# Revit family: Power-ModularDevices-GEWISS-90AM-CONTACTORS_MANUAL_COMMAND_20A
name_source: partatom
category: Apparecchi elettrici
revit_build: Autodesk Revit 2016 (Build: 20161004_0715(x64)
units: mm (PartAtom-declared; Revit-internal decimal feet)

## family parameters
Condiviso = No
Host = Superficie
Mantenere orientamento annotazione = Sì
Numero OmniClass = 23.80.30.00
Punto di calcolo locali = Sì
Quota connettore circolare = Usa diametro
Taglio con vuoti quando caricato = No
Tipo di parte = Normale
Titolo OmniClass = Distribution Devices

## types (4) — shared parameters
A = 18 mm  [stored 0.0590551 ft]
B = 85 mm  [stored 0.278871 ft]
C = 65 mm  [stored 0.213255 ft]
Catalogue = POWER
Catalogue Range = 90 AM
Control = Manual
D = 45 mm  [stored 0.147638 ft]
Electrocod = 1712
Fin_Amperometro = <Per categoria>
IDF = 7106f995-c053-4fad-b690-0f915b23fb57
IDT = 203b0cdd-a3f8-4527-9efa-be9d5b2ce0ff
Immagine tipo = GWD6744.jpg
No. Chorus modules = 1
Numero poli = 1
Potenza in Watt = 0 V
Produttore = GEWISS S.p.A.
Prospetto di default = 1219 mm
Rated current (AC-1/AC-7a) = 20 A - CTRM20
TEXT LABEL = A
Technical sheet = https://www.gewiss.com
URL = https://www.gewiss.com
Version file RFA = 18.0

## per-type parameters (varying)
| type | Control coil voltage (V) | Descrizione | EAN code | Modello |
| GWD6741 - CONTACTOR D/N 20A 2NO 24V 1M | 24Vac | CONTACTOR D/N 20A 2NO 24V 1M | 8011564809383 | GWD6741 |
| GWD6742 - CONTACTOR D/N 20A 2NO 230V 1M | 230Vac | CONTACTOR D/N 20A 2NO 230V 1M | 8011564809390 | GWD6742 |
| GWD6743 - CONTACTOR D/N 20A 2NC 230V 1M | 230Vac | CONTACTOR D/N 20A 2NC 230V 1M | 8011564809406 | GWD6743 |
| GWD6744 - CONTACTOR D/N 20A 1NO+1NC 230V 1M | 230Vac | CONTACTOR D/N 20A 1NO+1NC 230V 1M | 8011564809413 | GWD6744 |

note: [stored X ft] marks values corroborated as IEEE doubles in the binary element streams (Revit-internal decimal feet)
